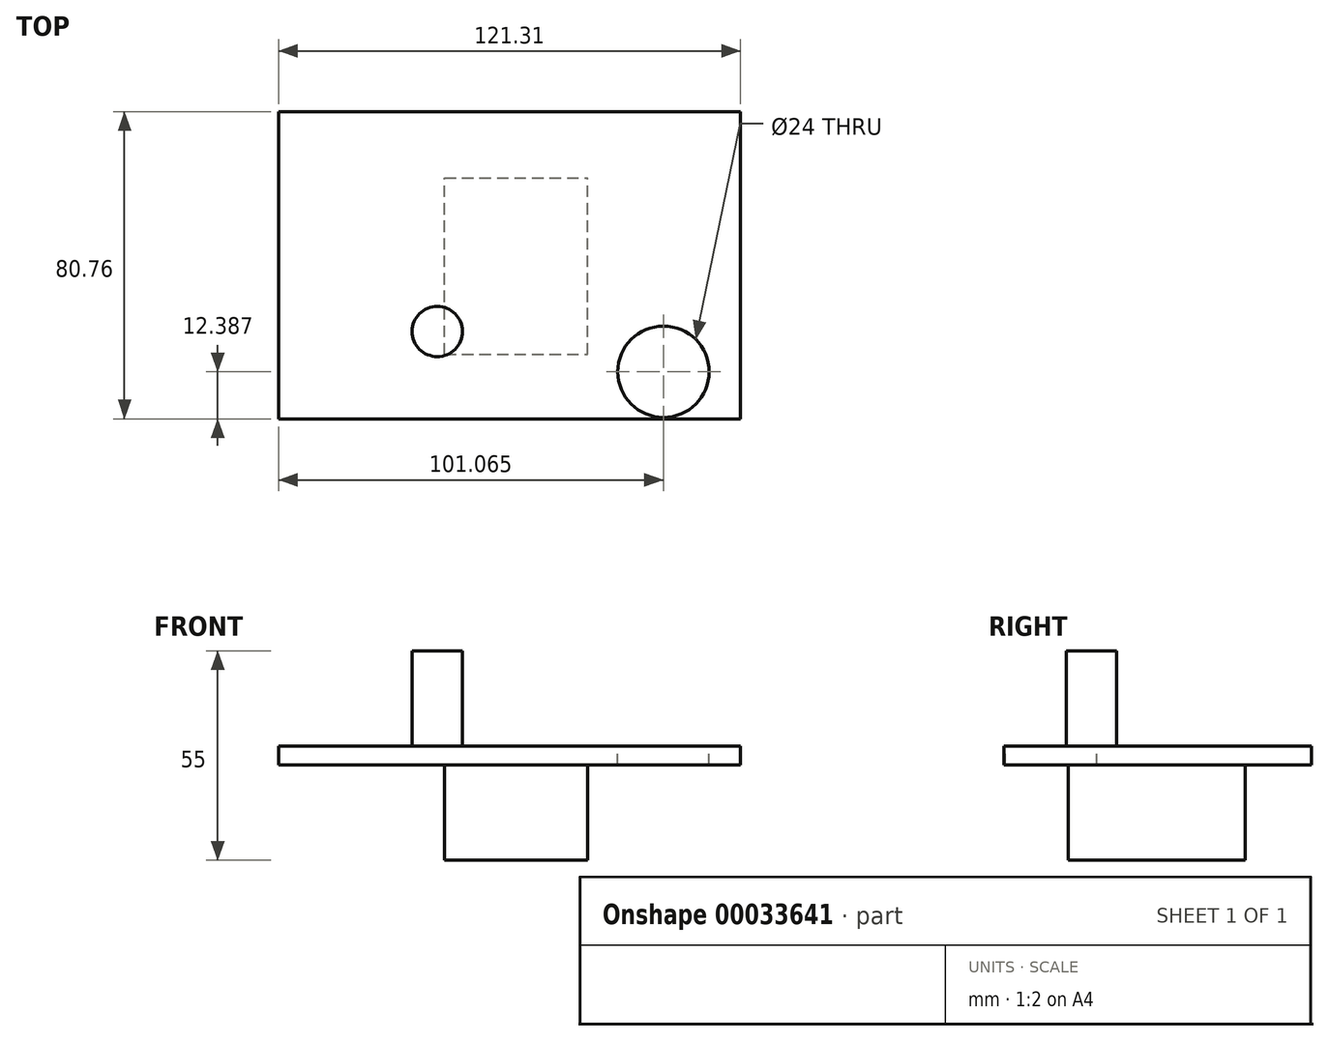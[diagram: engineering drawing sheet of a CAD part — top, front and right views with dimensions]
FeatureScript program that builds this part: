
annotation { "Feature Type Name" : "Feature", "Feature Type Description" : "" }
export const myFeature = defineFeature(function(context is Context, id is Id, definition is map)
    precondition{}
    {
        {
            var Q0;
            Q0=qCreatedBy(makeId("Top.planeOp"),FACE);
            var sketch = newSketch(context, id + "F0", { "sketchPlane" : qUnion([Q0])});
            skLineSegment(sketch, "E0.bottom", {"start": v(-37.62, -46.45) * mm, "end": v(0, -46.45) * mm});
            skLineSegment(sketch, "E0.top", {"start": v(-37.62, 0) * mm, "end": v(0, 0) * mm});
            skLineSegment(sketch, "E0.left", {"start": v(-37.62, -46.45) * mm, "end": v(-37.62, 0) * mm});
            skLineSegment(sketch, "E0.right", {"start": v(0, -46.45) * mm, "end": v(0, 0) * mm});
            skSolve(sketch);
        }
        {
            var Q0;
            Q0=makeQuery(id+"F0.imprint","IMPRINT",FACE,{"disambiguationData":[TD([[makeQuery(id+"F0.imprint","IMPRINT",EDGE,{"derivedFrom":sQuery(id+"F0.wireOp",EDGE,"E0.bottom")}),1.0]])]});
            extrude(context, id + "F1", {"entities" : qUnion([Q0]), "depth" : 25 * mm});
        }
        {
            var Q0;
            Q0=makeQuery(id+"F1.opExtrude","CAP_FACE",FACE,{"disambiguationData":[OSD([sQuery(id+"F0.wireOp",EDGE,"E0.bottom"),sQuery(id+"F0.wireOp",EDGE,"E0.top"),sQuery(id+"F0.wireOp",EDGE,"E0.left"),sQuery(id+"F0.wireOp",EDGE,"E0.right")])],"isStart":false});
            var sketch = newSketch(context, id + "F2", { "sketchPlane" : qUnion([Q0])});
            skLineSegment(sketch, "E1.rect.bottom", {"start": v(-81.17, -63.38) * mm, "end": v(40.14, -63.38) * mm});
            skLineSegment(sketch, "E1.rect.top", {"start": v(-81.17, 17.38) * mm, "end": v(40.14, 17.38) * mm});
            skLineSegment(sketch, "E1.rect.left", {"start": v(-81.17, -63.38) * mm, "end": v(-81.17, 17.38) * mm});
            skLineSegment(sketch, "E1.rect.right", {"start": v(40.14, -63.38) * mm, "end": v(40.14, 17.38) * mm});
            skPoint(sketch, "E1.rect.middle", {"position": v(-20.51, -23) * mm});
            skSolve(sketch);
        }
        {
            var Q0;
            Q0 = qSketchRegion(id + "F2", true);
            extrude(context, id + "F3", {"entities" : qUnion([Q0]), "operationType" : NewBodyOperationType.ADD, "depth" : 5 * mm});
        }
        {
            var Q0;
            Q0=makeQuery(id+"F3.opExtrude","CAP_FACE",FACE,{"disambiguationData":[OSD([sQuery(id+"F2.wireOp",EDGE,"E1.rect.bottom"),sQuery(id+"F2.wireOp",EDGE,"E1.rect.top"),sQuery(id+"F2.wireOp",EDGE,"E1.rect.left"),sQuery(id+"F2.wireOp",EDGE,"E1.rect.right")])],"isStart":false});
            var sketch = newSketch(context, id + "F4", { "sketchPlane" : qUnion([Q0])});
            skCircle(sketch, "E2", {"center": v(-39.5, -40.4) * mm, "radius": 6.6 * mm});
            skSolve(sketch);
        }
        {
            var Q0;
            Q0 = qSketchRegion(id + "F4", true);
            extrude(context, id + "F5", {"entities" : qUnion([Q0]), "operationType" : NewBodyOperationType.ADD, "depth" : 25 * mm});
        }
        {
            var Q0;
            Q0=makeQuery(id+"F3.opExtrude","CAP_FACE",FACE,{"disambiguationData":[OSD([sQuery(id+"F2.wireOp",EDGE,"E1.rect.bottom"),sQuery(id+"F2.wireOp",EDGE,"E1.rect.top"),sQuery(id+"F2.wireOp",EDGE,"E1.rect.left"),sQuery(id+"F2.wireOp",EDGE,"E1.rect.right")])],"isStart":false});
            var sketch = newSketch(context, id + "F6", { "sketchPlane" : qUnion([Q0])});
            skCircle(sketch, "E3", {"center": v(19.9, -51) * mm, "radius": 6 * mm});
            skSolve(sketch);
        }
        {
            var Q0;
            Q0=sQuery(id+"F6.wireOp",VERTEX,"E3.center");
            var Q1;
            Q1=makeQuery(id+"F1.opExtrude","SWEPT_BODY",BODY,{"disambiguationData":[OSD([sQuery(id+"F0.wireOp",EDGE,"E0.bottom"),sQuery(id+"F0.wireOp",EDGE,"E0.top"),sQuery(id+"F0.wireOp",EDGE,"E0.left"),sQuery(id+"F0.wireOp",EDGE,"E0.right")])]});
            hole(context, id + "F7", {"style" : HoleStyle.SIMPLE, "holeDiameter" : 24 * mm, "endStyle" : HoleEndStyle.THROUGH, "locations" : qUnion([Q0]), "scope" : qUnion([Q1])});
        }
    });
